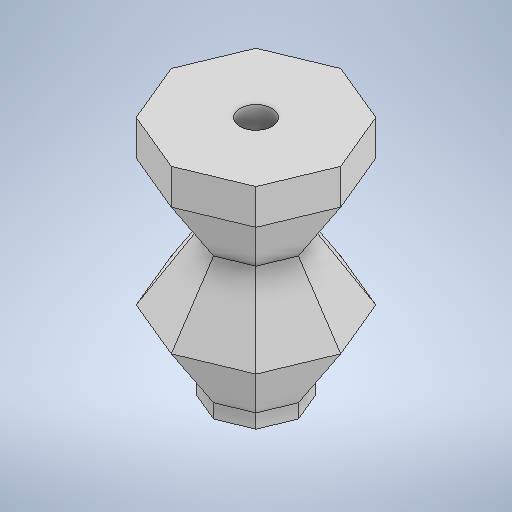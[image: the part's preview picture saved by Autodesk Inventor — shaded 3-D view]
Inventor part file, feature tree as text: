
AUTODESK INVENTOR PART (.ipt)
format: ipt  version: 2025.1 (Build 291241000, 241)  size: 316,416 bytes
history: native  units: mm
features: sketch x5, other x3, extrude x3, mirror x2, projected_geometry x2, loft x1, shell x1
ambient origin geometry x8: Origin, YZ Plane, XZ Plane, XY Plane, X Axis, Y Axis, Z Axis, Center Point
bodies: Body1 (feature_tree)
feature tree (17):
  other  "솔리드1"
  sketch  "스케치1"
  other  "작업 평면1"
  loft  "로프트1"
  other  "작업 평면2"
  mirror  "미러1"
  mirror  "미러2"
  shell  "쉘1"  Thickness=9.0mm
  extrude  "돌출1"  Depth=12.0mm
  extrude  "돌출2"  TaperAngle=0.0deg  [1 undecoded]
  extrude  "돌출3"  TaperAngle=0.0deg  [1 undecoded]
  sketch  "스케치2"
  sketch  "스케치3"
  projected_geometry  "투영된 루프1"
  sketch  "스케치4"
  projected_geometry  "투영된 루프2"
  sketch  "스케치5"
note: 2 required parameter values undecoded (feature->parameter linkage not recoverable at this tier; creation-order binding heuristic only, values carry confidence <= 0.55)
